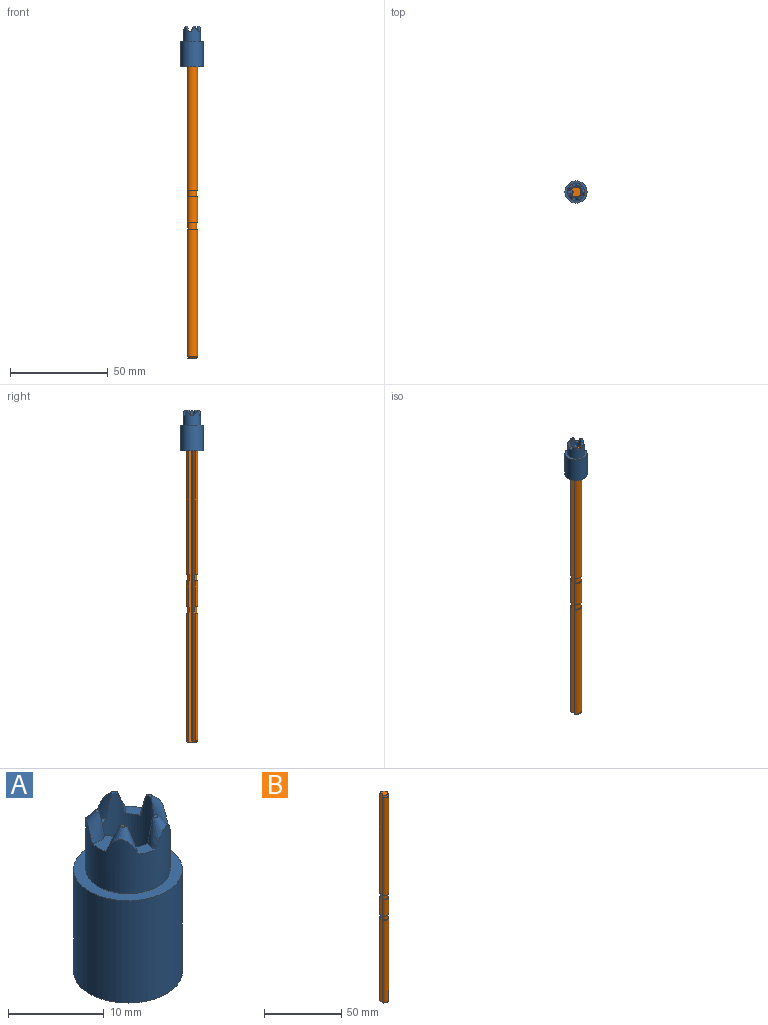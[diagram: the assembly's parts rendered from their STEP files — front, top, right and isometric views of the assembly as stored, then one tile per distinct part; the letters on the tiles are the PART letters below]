
ASSEMBLY  parts=2 mates=1
PART A: 25 faces, bbox 11.7x11.7x21.3 mm
  f0: cone r=1.8mm half-angle=24.8deg, axis (0.34,0,-0.94), area 9mm2, adj f1,f2,f3,f4,f21
  f1: plane 0.97x0.71mm, normal (0,0,1), area 0.2mm2, adj f0,f2
  f2: cylinder r=3.06mm len=20.85mm, axis (0,0,-1), area 308.4mm2, adj f0,f1,f4,f5,f6,f7,f8,f9
  f3: cylinder r=4.4mm len=8.8mm, axis (0,0,-1), area 159.2mm2, adj f0,f4,f6,f7,f11,f12,f16,f17
  f4: plane 2.32x2.22mm, normal (0,0,1), area 2.2mm2, adj f0,f2,f3,f6
  f5: plane 0.97x0.81mm, normal (0,0,1), area 0.2mm2, adj f2,f6
  f6: cone r=1.8mm half-angle=24.8deg, axis (0.11,0.33,-0.94), area 9mm2, adj f2,f3,f4,f5,f7
  f7: plane 2.2x1.91mm, normal (0,0,1), area 2.2mm2, adj f2,f3,f6,f11
  f8: plane 0.63x0.58mm, normal (0,0,1), area 0.2mm2, adj f2,f11
  f9: cylinder r=0.15mm len=20.77mm, axis (0,0,-1), area 4mm2, adj f2,f10,f11,f23
  f10: plane 20.17x0.68mm, normal (0.71,0.71,0), area 17.7mm2, adj f9,f11,f12,f20,f23
  f11: cone r=1.8mm half-angle=24.8deg, axis (-0.28,0.2,-0.94), area 9.8mm2, adj f2,f3,f7,f8,f9,f10,f12
  f12: plane 2.7x2.17mm, normal (0,0,1), area 4.4mm2, adj f3,f10,f11,f14,f16,f20
  f13: plane 0.63x0.58mm, normal (0,0,1), area 0.2mm2, adj f2,f16
  f14: plane 20.17x0.68mm, normal (0.71,-0.71,0), area 17.7mm2, adj f12,f15,f16,f20,f23
  f15: cylinder r=0.15mm len=20.77mm, axis (0,0,-1), area 4mm2, adj f2,f14,f16,f23
  f16: cone r=1.8mm half-angle=24.8deg, axis (-0.28,-0.2,-0.94), area 9.8mm2, adj f2,f3,f12,f13,f14,f15,f17
  f17: plane 2.2x1.91mm, normal (0,0,1), area 2.2mm2, adj f2,f3,f16,f18
  f18: cone r=1.8mm half-angle=24.8deg, axis (0.11,-0.33,-0.94), area 9mm2, adj f2,f3,f17,f19,f21
  f19: plane 0.97x0.81mm, normal (0,0,1), area 0.2mm2, adj f2,f18
  f20: cylinder r=0.9mm len=17.97mm, axis (0,0,-1), area 25.4mm2, adj f10,f12,f14,f23
  f21: plane 2.32x2.22mm, normal (0,0,1), area 2.2mm2, adj f0,f2,f3,f18
  f22: cylinder r=5.68mm len=13.05mm, axis (0,0,1), area 465.3mm2, adj f23,f24
  f23: plane 11.35x11.35mm, normal (0,0,-1), area 74.2mm2, adj f2,f9,f10,f14,f15,f20,f22
  f24: plane 11.35x11.35mm, normal (0,0,1), area 40.4mm2, adj f3,f22
PART B: 16 faces, bbox 5.6x5.9x165 mm
  f0: cylinder r=2.95mm len=13.2mm, axis (0,0,-1), area 201.2mm2, adj f2,f4,f11,f15
  f1: cylinder r=2.95mm len=65.4mm, axis (0,0,-1), area 996.7mm2, adj f2,f4,f8,f12
  f2: plane 165.02x1.36mm, normal (-0.71,0.71,0), area 307.8mm2, adj f0,f1,f3,f5,f6,f7,f8,f9
  f3: cylinder r=2.95mm len=77.7mm, axis (0,0,-1), area 1184.2mm2, adj f2,f4,f9,f14
  f4: plane 165.02x1.36mm, normal (-0.71,-0.71,0), area 307.8mm2, adj f0,f1,f3,f5,f6,f7,f8,f9
  f5: cylinder r=0.3mm len=165mm, axis (0,0,-1), area 77.8mm2, adj f2,f4,f6,f7
  f6: plane 5.09x4.75mm, normal (0,0,1), area 18.2mm2, adj f2,f4,f5,f9
  f7: plane 4.69x4.41mm, normal (0,0,-1), area 15.6mm2, adj f2,f4,f5,f8
  f8: cone r=2.95mm half-angle=45deg, axis (0,0,1), area 11.7mm2, adj f1,f2,f4,f7
  f9: cone r=2.54mm half-angle=15deg, axis (0,0,-1), area 22.2mm2, adj f2,f3,f4,f6
  f10: cylinder r=2.4mm len=4.8mm, axis (0,0,-1), area 41.8mm2, adj f2,f4,f11,f12
  f11: plane 5.89x5.45mm, normal (0,0,-1), area 7.6mm2, adj f0,f2,f4,f10
  f12: plane 5.89x5.45mm, normal (0,0,1), area 7.6mm2, adj f1,f2,f4,f10
  f13: cylinder r=2.4mm len=4.8mm, axis (0,0,-1), area 41.8mm2, adj f2,f4,f14,f15
  f14: plane 5.89x5.45mm, normal (0,0,-1), area 7.6mm2, adj f2,f3,f4,f13
  f15: plane 5.89x5.45mm, normal (0,0,1), area 7.6mm2, adj f0,f2,f4,f13
PLACE A at identity fixed
PLACE B t=(0,0,-162.15)mm
MATE fastened B.f0 <-> A.f2  axis (0,0,1) through (0,0,2.85)mm
